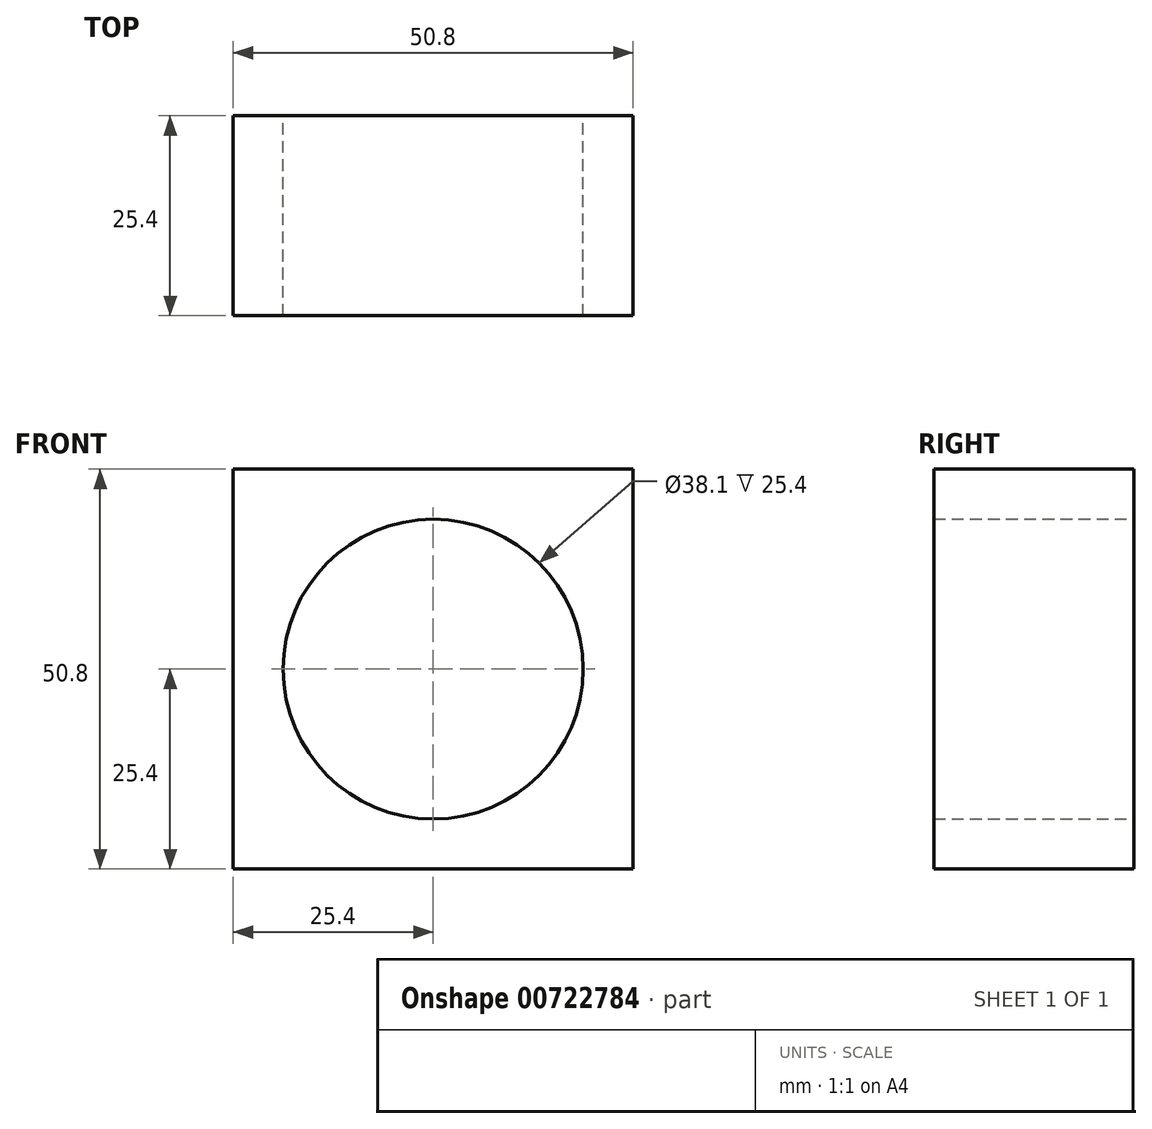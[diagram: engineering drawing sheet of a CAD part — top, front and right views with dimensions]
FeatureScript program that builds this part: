
annotation { "Feature Type Name" : "Feature", "Feature Type Description" : "" }
export const myFeature = defineFeature(function(context is Context, id is Id, definition is map)
    precondition{}
    {
        {
            var Q0;
            Q0=qCreatedBy(makeId("Front.planeOp"),FACE);
            var sketch = newSketch(context, id + "F0", { "sketchPlane" : qUnion([Q0])});
            skLineSegment(sketch, "E0.bottom", {"start": v(0, 0) * mm, "end": v(50.8, 0) * mm});
            skLineSegment(sketch, "E0.top", {"start": v(0, 50.8) * mm, "end": v(50.8, 50.8) * mm});
            skLineSegment(sketch, "E0.left", {"start": v(0, 0) * mm, "end": v(0, 50.8) * mm});
            skLineSegment(sketch, "E0.right", {"start": v(50.8, 0) * mm, "end": v(50.8, 50.8) * mm});
            skCircle(sketch, "E1", {"center": v(25.4, 25.4) * mm, "radius": 19.05 * mm});
            skSolve(sketch);
        }
        {
            var Q0;
            Q0=makeQuery(id+"F0.imprint","IMPRINT",FACE,{"disambiguationData":[TD([[makeQuery(id+"F0.imprint","IMPRINT",EDGE,{"derivedFrom":sQuery(id+"F0.wireOp",EDGE,"E0.bottom")}),1.0]])]});
            extrude(context, id + "F1", {"entities" : qUnion([Q0]), "depth" : 25.4 * mm, "offsetDistance" : 25.4 * mm});
        }
    });
